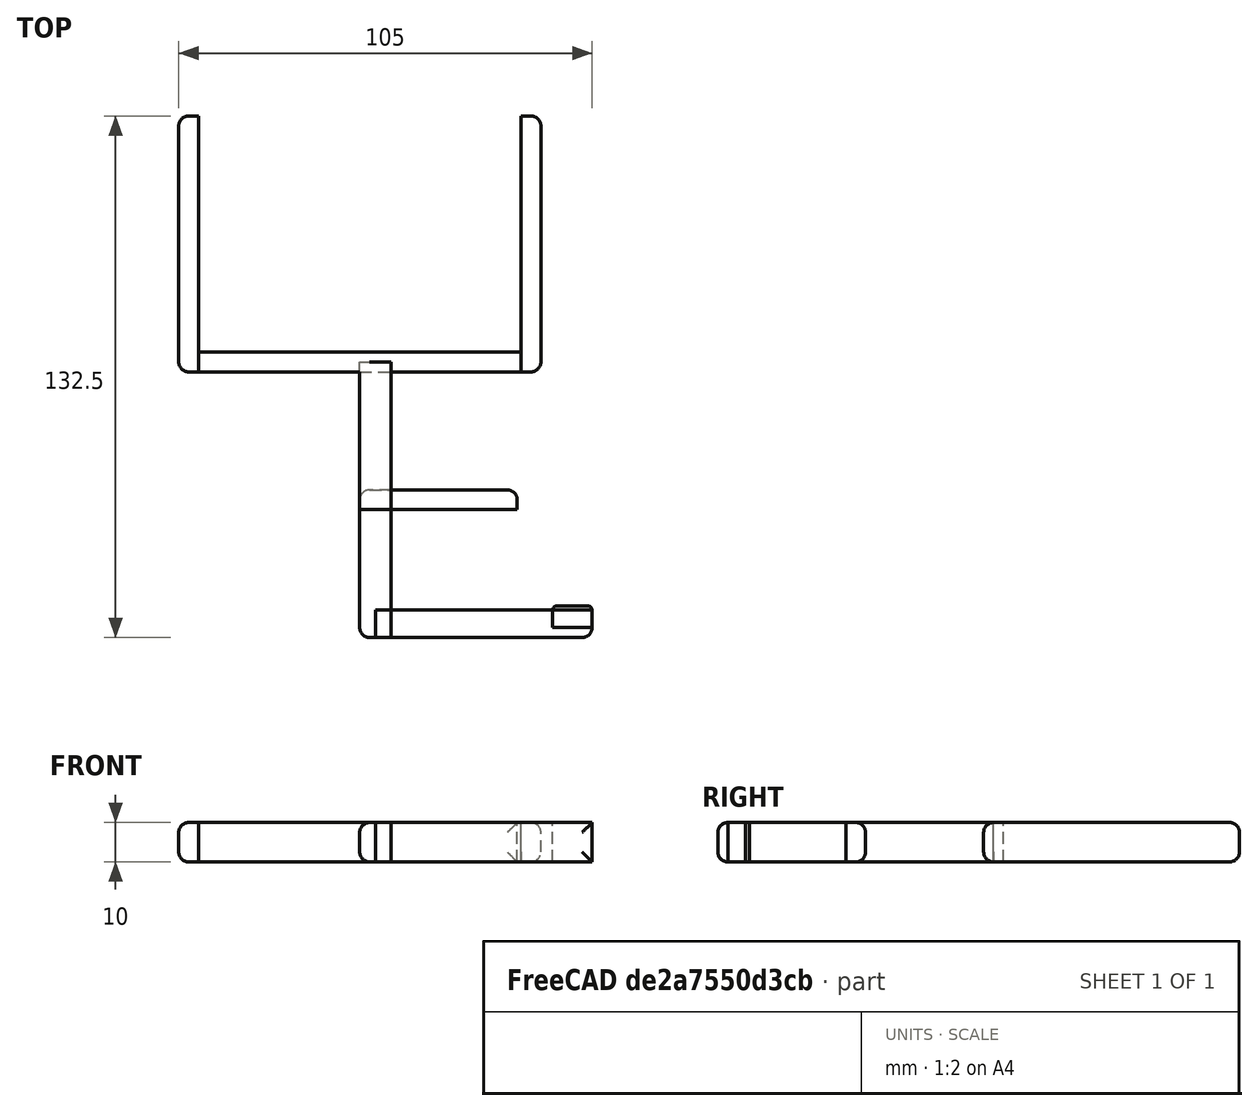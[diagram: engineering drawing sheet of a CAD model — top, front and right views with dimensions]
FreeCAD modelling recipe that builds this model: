
FCSTD DOCUMENT  (FreeCAD 0.21R33771 (Git))
Label: heating-tabel-clip
License: All rights reserved
LicenseURL: http://en.wikipedia.org/wiki/All_rights_reserved
objects: Part::Fillet×14, Part::Box×7
note: 21 computed .brp shape members not serialized (recipe doc carries the construction recipe); baked Part::Feature solids carry a one-line shape summary decoded from their .brp

FEATURE [Part::Box] Box  label="base"
  AttacherType = Attacher::AttachEngine3D
  Height = 10
  Length = 82
  Placement = pos=(0,35,0) rot=(0,0,1;0rad)
  Width = 5
FEATURE [Part::Box] Box001  label="stand"
  AttacherType = Attacher::AttachEngine3D
  Height = 10
  Length = 8
  Placement = pos=(41,-32.5,0) rot=(0,0,1;0rad)
  Width = 70
FEATURE [Part::Box] Box002  label="clip-top"
  AttacherType = Attacher::AttachEngine3D
  Height = 10
  Length = 40
  Placement = pos=(41,0,0) rot=(0,0,1;0rad)
  Width = 5
FEATURE [Part::Box] Box003  label="clip-down"
  AttacherType = Attacher::AttachEngine3D
  Height = 10
  Length = 55
  Placement = pos=(45,-32.5,0) rot=(0,0,1;0rad)
  Width = 7
FEATURE [Part::Box] Box004  label="Cube"
  AttacherType = Attacher::AttachEngine3D
  Height = 10
  Length = 10
  Placement = pos=(90,-30,0) rot=(0,0,1;0rad)
  Width = 5.5
FEATURE [Part::Box] Box005  label="front-wall"
  AttacherType = Attacher::AttachEngine3D
  Height = 10
  Length = 5
  Placement = pos=(-5,35,0) rot=(0,0,1;0rad)
  Width = 65
FEATURE [Part::Box] Box006  label="Cube002"
  AttacherType = Attacher::AttachEngine3D
  Height = 10
  Length = 5
  Placement = pos=(82,35,0) rot=(0,0,1;0rad)
  Width = 65
FEATURE [Part::Fillet] Fillet
  Base = -> Box005
  Edges = 1 edges r=2.5: [Edge1]
FEATURE [Part::Fillet] Fillet001
  Base = -> Box001
  Edges = 1 edges r=2.5: [Edge1]
FEATURE [Part::Fillet] Fillet002
  Base = -> Box006
  Edges = 1 edges r=2.5: [Edge7]
FEATURE [Part::Fillet] Fillet003
  Base = -> Fillet
  Edges = 1 edges r=2.5: [Edge4]
FEATURE [Part::Fillet] Fillet004
  Base = -> Fillet003
  Edges = 2 edges r=2.5: [Edge1,Edge3]
FEATURE [Part::Fillet] Fillet005
  Base = -> Box
  Edges = 2 edges r=2.5: [Edge9,Edge10]
FEATURE [Part::Fillet] Fillet006
  Base = -> Fillet002
  Edges = 2 edges r=2.5: [Edge7,Edge11]
FEATURE [Part::Fillet] Fillet007
  Base = -> Fillet006
  Edges = 2 edges r=2.5: [Edge1,Edge5]
FEATURE [Part::Fillet] Fillet008
  Base = -> Fillet001
  Edges = 2 edges r=2.5: [Edge1,Edge3]
FEATURE [Part::Fillet] Fillet009
  Base = -> Box002
  Edges = 2 edges r=2.5: [Edge2,Edge4]
FEATURE [Part::Fillet] Fillet010
  Base = -> Fillet009
  Edges = 3 edges r=2.5: [Edge14,Edge15,Edge16]
FEATURE [Part::Fillet] Fillet011
  Base = -> Box003
  Edges = 3 edges r=2.5: [Edge5,Edge9,Edge10]
FEATURE [Part::Fillet] Fillet012
  Base = -> Box004
  Edges = 1 edges r=1: [Edge7]
FEATURE [Part::Fillet] Fillet013
  Base = -> Fillet012
  Edges = 1 edges r=1: [Edge15]
